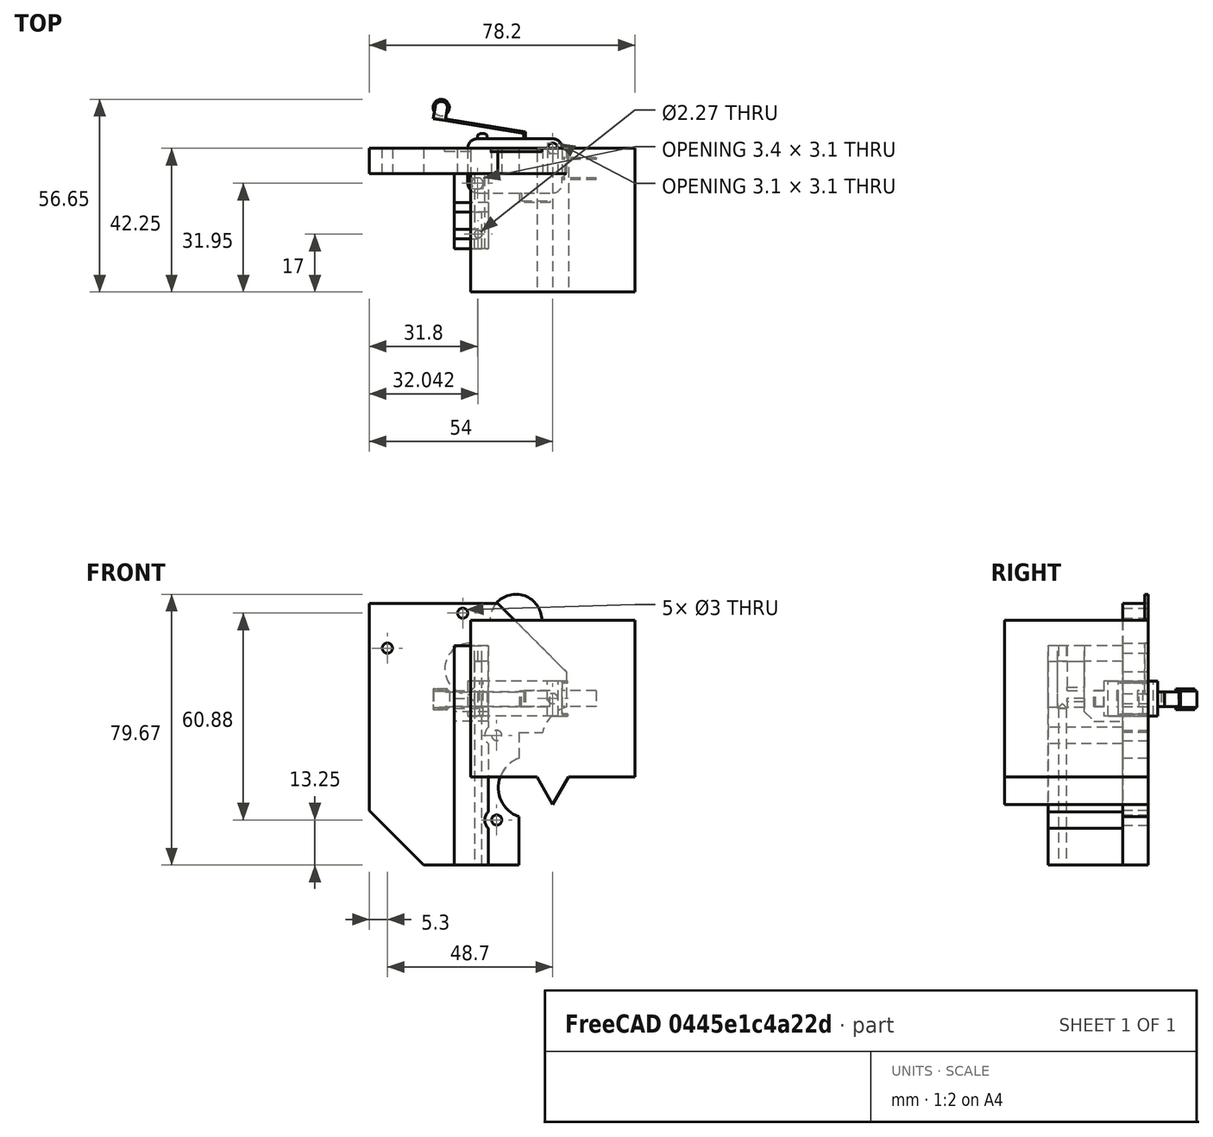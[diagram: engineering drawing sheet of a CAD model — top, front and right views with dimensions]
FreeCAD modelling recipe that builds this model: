
FCSTD DOCUMENT  (FreeCAD 0.19R22284 (Git))
Label: no_touchy
License: All rights reserved
LicenseURL: http://en.wikipedia.org/wiki/All_rights_reserved
objects: PartDesign::CoordinateSystem×15, Sketcher::SketchObject×14, PartDesign::Pad×6, PartDesign::Pocket×6, App::Part×6, App::Link×5, App::DocumentObjectGroup×2, Part::Feature×2, PartDesign::Body×2, PartDesign::Chamfer×2, App::FeaturePython×1, PartDesign::AdditivePipe×1, Spreadsheet::Sheet×1, Mesh::Feature×1
note: 63 computed .brp shape members not serialized (recipe doc carries the construction recipe); baked Part::Feature solids carry a one-line shape summary decoded from their .brp

FEATURE [PartDesign::CoordinateSystem] LCS_Origin
  AttacherType = Attacher::AttachEngine3D
  MapMode = 2
  Support = -> [X_Axis]
FEATURE [App::DocumentObjectGroup] Constraints
FEATURE [App::FeaturePython] Variables  # WARN: FeaturePython — macro-defined, semantics opaque (R4)
FEATURE [PartDesign::CoordinateSystem] LCS_0
  AttacherType = Attacher::AttachEngine3D
  MapMode = 2
  Support = -> [X_Axis001]
FEATURE [Sketcher::SketchObject] Sketch  label="hex"
  MapMode = 5
  Placement = pos=(0,0,0) rot=(0.57735,0.57735,0.57735;2.0944rad)
  expr: Constraints[19] = Spreadsheet.allen_key_hex
  sketch-geometry (7):
    g0: LineSegment StartX=0 StartY=0.733235 StartZ=0 EndX=-0.635 EndY=0.366617 EndZ=0
    g1: LineSegment StartX=-0.635 StartY=0.366617 StartZ=0 EndX=-0.635 EndY=-0.366617 EndZ=0
    g2: LineSegment StartX=-0.635 StartY=-0.366617 StartZ=0 EndX=0 EndY=-0.733235 EndZ=0
    g3: LineSegment StartX=0 StartY=-0.733235 StartZ=0 EndX=0.635 EndY=-0.366617 EndZ=0
    g4: LineSegment StartX=0.635 StartY=-0.366617 StartZ=0 EndX=0.635 EndY=0.366617 EndZ=0
    g5: LineSegment StartX=0.635 StartY=0.366617 StartZ=0 EndX=0 EndY=0.733235 EndZ=0
    g6: Circle [constr] CenterX=0 CenterY=0 CenterZ=0 NormalX=0 NormalY=0 NormalZ=1 AngleXU=0 Radius=0.733235
  constraints (16):
    c: Coincident(g0,g1)
    c: Coincident(g1,g2)
    c: Coincident(g2,g3)
    c: Coincident(g3,g4)
    c: Coincident(g4,g5)
    c: Coincident(g5,g0)
    c: Equal(g0, g1-g5) x5
    c: PointOnObject(g0,g6)
    c: PointOnObject(g1,g6)
    c: PointOnObject(g2,g6)
    c: PointOnObject(g3,g6)
    c: PointOnObject(g4,g6)
    c: PointOnObject(g5,g6)
    c: Coincident(g6,g-1)
    c: Vertical(g0,g-1)
    c: Distance(g3,g1) = 1.27
FEATURE [Sketcher::SketchObject] Sketch001  label="path"
  MapMode = 5
  expr: Constraints[5] = Spreadsheet.allen_key_long
  expr: Constraints[4] = Spreadsheet.allen_key_short
  sketch-geometry (3):
    g0: LineSegment StartX=0 StartY=-1.3e-15 StartZ=0 EndX=-12.3 EndY=-1.3e-15 EndZ=0
    g1: LineSegment StartX=-15.3 StartY=-3 StartZ=0 EndX=-15.3 EndY=-73.5 EndZ=0
    g2: ArcOfCircle CenterX=-12.3 CenterY=-3 CenterZ=0 NormalX=0 NormalY=0 NormalZ=1 AngleXU=0 Radius=3 StartAngle=1.5708 EndAngle=3.14159
  constraints (8):
    c: Coincident(g-1,g0)
    c: Vertical(g1)
    c: Tangent(g0,g2) = -1.5708
    c: Tangent(g1,g2) = -1.5708
    c: DistanceX(g1,g0) = 15.3
    c: DistanceY(g1,g0) = 73.5
    c: Horizontal(g0)
    c: Radius(g2) = 3
FEATURE [PartDesign::AdditivePipe] AdditivePipe
  AuxilleryCurvelinear = true
  AuxillerySpineTangent = false
  Binormal = (0,0,0)
  Mode = 0
  Placement = pos=(0,0,0) rot=(0.57735,0.57735,0.57735;2.0944rad)
  Profile = -> Sketch
  Spine = -> Sketch001
  SpineTangent = false
  Transformation = 0
  Transition = 0
FEATURE [Sketcher::SketchObject] Sketch002
  MapMode = 5
  Placement = pos=(0,0,0) rot=(1,0,0;1.5708rad)
  sketch-geometry (10):
    g0: LineSegment StartX=60 StartY=0 StartZ=0 EndX=0 EndY=0 EndZ=0
    g1: LineSegment StartX=0 StartY=0 StartZ=0 EndX=0 EndY=36.25 EndZ=0
    g2: LineSegment StartX=6.5 StartY=42.75 StartZ=0 EndX=11.5 EndY=42.75 EndZ=0
    g3: LineSegment StartX=18 StartY=49.25 StartZ=0 EndX=18 EndY=87.75 EndZ=0
    g4: LineSegment StartX=21 StartY=90.75 StartZ=0 EndX=57 EndY=90.75 EndZ=0
    g5: LineSegment StartX=60 StartY=87.75 StartZ=0 EndX=60 EndY=0 EndZ=0
    g6: ArcOfCircle CenterX=6.5 CenterY=36.25 CenterZ=0 NormalX=0 NormalY=0 NormalZ=1 AngleXU=0 Radius=6.5 StartAngle=1.5708 EndAngle=3.14159
    g7: ArcOfCircle CenterX=11.5 CenterY=49.25 CenterZ=0 NormalX=0 NormalY=0 NormalZ=1 AngleXU=0 Radius=6.5 StartAngle=4.71239 EndAngle=6.28319
    g8: ArcOfCircle CenterX=21 CenterY=87.75 CenterZ=0 NormalX=0 NormalY=0 NormalZ=1 AngleXU=0 Radius=3 StartAngle=1.5708 EndAngle=3.14159
    g9: ArcOfCircle CenterX=57 CenterY=87.75 CenterZ=0 NormalX=0 NormalY=0 NormalZ=1 AngleXU=0 Radius=3 StartAngle=1.2e-15 EndAngle=1.5708
  constraints (25):
    c: Horizontal(g0)
    c: Coincident(g0,g1)
    c: Vertical(g1)
    c: Horizontal(g2)
    c: Vertical(g3)
    c: Horizontal(g4)
    c: Coincident(g5,g0)
    c: Vertical(g5)
    c: Tangent(g2,g6) = 1.5708
    c: Tangent(g1,g6) = 1.5708
    c: Tangent(g2,g7) = -1.5708
    c: Tangent(g3,g7) = -1.5708
    c: DistanceY(g0,g2) = 42.75
    c: DistanceX(g1,g3) = 18
    c: DistanceX(g2,g2) = 5
    c: Equal(g6,g7)
    c: Coincident(g0,g-1)
    c: Tangent(g4,g8) = 1.5708
    c: Tangent(g3,g8) = 1.5708
    c: DistanceY(g2,g4) = 48
    c: Radius(g8) = 3
    c: Tangent(g4,g9) = 1.5708
    c: Tangent(g5,g9) = 1.5708
    c: Equal(g8,g9)
    c: DistanceX(g3,g5) = 42
FEATURE [PartDesign::Pad] Pad
  Length = 3.2
  Length2 = 100
  Placement = pos=(0,0,0) rot=(1,0,0;1.5708rad)
  Profile = -> Sketch002
  Type = 0
FEATURE [Sketcher::SketchObject] Sketch003
  ExternalGeometry = -> [Pad]
  MapMode = 5
  Placement = pos=(0,-3.2,1.1e-15) rot=(1,0,0;1.5708rad)
  Support = -> [Pad]
  sketch-geometry (8):
    g0: Circle CenterX=19.19 CenterY=39.94 CenterZ=0 NormalX=0 NormalY=0 NormalZ=1 AngleXU=0 Radius=1.19
    g1: Circle CenterX=2.69 CenterY=29.07 CenterZ=0 NormalX=0 NormalY=0 NormalZ=1 AngleXU=0 Radius=1.19
    g2: Circle CenterX=2.69 CenterY=4.19 CenterZ=0 NormalX=0 NormalY=0 NormalZ=1 AngleXU=0 Radius=1.19
    g3: LineSegment [constr] StartX=2.69 StartY=3 StartZ=0 EndX=2.69 EndY=0 EndZ=0
    g4: LineSegment [constr] StartX=2.69 StartY=27.88 StartZ=0 EndX=2.69 EndY=5.38 EndZ=0
    g5: LineSegment [constr] StartX=1.5 StartY=29.07 StartZ=0 EndX=0 EndY=29.07 EndZ=0
    g6: LineSegment [constr] StartX=18 StartY=39.94 StartZ=0 EndX=0 EndY=39.94 EndZ=0
    g7: LineSegment [constr] StartX=19.19 StartY=90.75 StartZ=0 EndX=19.19 EndY=38.75 EndZ=0
  constraints (29):
    c: Diameter(g0) = 2.38
    c: Equal(g0,g1)
    c: Equal(g1,g2)
    c: Vertical(g2,g1)
    c: Vertical(g3)
    c: Horizontal(g3,g-1)
    c: Vertical(g3,g2)
    c: PointOnObject(g3,g2)
    c: Distance(g3) = 3
    c: Vertical(g4)
    c: Distance(g4) = 22.5
    c: PointOnObject(g4,g2)
    c: Vertical(g4,g2)
    c: PointOnObject(g4,g1)
    c: Horizontal(g5)
    c: Horizontal(g5,g1)
    c: PointOnObject(g5,g1)
    c: Distance(g5) = 1.5
    c: PointOnObject(g5,g-3)
    c: Horizontal(g6)
    c: PointOnObject(g6,g0)
    c: Horizontal(g6,g0)
    c: Distance(g6) = 18
    c: Vertical(g6,g-3)
    c: Vertical(g7)
    c: Horizontal(g7,g-5)
    c: Distance(g7) = 52
    c: PointOnObject(g7,g0)
    c: Vertical(g0,g7)
FEATURE [PartDesign::Pocket] Pocket
  BaseFeature = -> Pad
  Length = 5
  Length2 = 100
  Placement = pos=(0,0,0) rot=(1,0,0;1.5708rad)
  Profile = -> Sketch003
  Type = 1
FEATURE [Part::Feature] Part__Feature001  label="V_166_1C25_ACTUATOR"
  Placement = pos=(-8.6,2.8,-0.2) rot=(0,0,1;0rad)
  shape: bbox 27.14 x 11.6 x 6 mm, 20 faces (baked)
FEATURE [Part::Feature] Part__Feature  label="V_166_1C25_BASE"
  shape: bbox 37.8 x 20.4 x 10.3 mm, 51 faces (baked)
FEATURE [Spreadsheet::Sheet] Spreadsheet
  cells = A1(limit_switch_mount_height)=5; A2(storage_ledge_height)=50; A3(probe_ledge_height)=25; A4(allen_key_long)=73.5; A5(allen_key_short)=15.3; A6(allen_key_hex)=1.27; A7(no_touchy_plate_mount_thickness)=7.5; A8(limit_switch_hole_offset_x)=-10; A9(limit_switch_hole_offset_y)=33; A10(no_touchy_allen_block_pad_height)=22; A11(no_touchy_allen_block_pad_length)=64.5; A12(no_touchy_allen_hole_length)=47.5; A13(no_touchy_allen_block_pad_width)=10; A14(no_touchy_allen_hole_diameter)==allen_key_hex + 1
FEATURE [PartDesign::CoordinateSystem] LCS_hole_1
  AttacherType = Attacher::AttachEngine3D
  AttachmentOffset = pos=(0,0,0) rot=(-0.57735,0.57735,-0.57735;2.0944rad)
  MapMode = 11
  Placement = pos=(0,0,-5.15) rot=(0,0.707107,-0.707107;3.14159rad)
  Support = -> [Part__Feature]
FEATURE [PartDesign::CoordinateSystem] LCS_hole_2
  AttacherType = Attacher::AttachEngine3D
  AttachmentOffset = pos=(0,0,0) rot=(0,-0.707107,0.707107;3.14159rad)
  MapMode = 45
  Placement = pos=(-22.2,-10.3,-5.15) rot=(0,-0.707107,0.707107;3.14159rad)
  Support = -> [Part__Feature]
FEATURE [PartDesign::CoordinateSystem] LCS_center
  AttacherType = Attacher::AttachEngine3D
  AttachmentOffset = pos=(0,0,0) rot=(0,0,1;3.14159rad)
  MapMode = 45
  Placement = pos=(-10.756,-5.10422,-5.15) rot=(0,0,1;4.67226rad)
  Support = -> [Part__Feature]
FEATURE [PartDesign::CoordinateSystem] LCS_allen_short_bottom_tip
  AttacherType = Attacher::AttachEngine3D
  MapMode = 45
  Placement = pos=(-1e-16,-0.635,-1e-16) rot=(0,0,1;0rad)
  Support = -> [AdditivePipe]
FEATURE [PartDesign::CoordinateSystem] LCS_allen_short_bottom_center
  AttacherType = Attacher::AttachEngine3D
  MapMode = 45
  Placement = pos=(-6.15,-0.635,-2e-16) rot=(0.57735,0.57735,0.57735;4.18879rad)
  Support = -> [AdditivePipe]
FEATURE [PartDesign::CoordinateSystem] LCS_allen_bottom_center
  AttacherType = Attacher::AttachEngine3D
  MapMode = 45
  Placement = pos=(-15.3,-73.5,-1.9e-15) rot=(0,0.707107,0.707107;3.14159rad)
  Support = -> [AdditivePipe]
FEATURE [Sketcher::SketchObject] Sketch004
  MapMode = 1
  Placement = pos=(0,0,0) rot=(1,0,0;1.5708rad)
  sketch-geometry (11):
    g0: LineSegment StartX=-24.2 StartY=23.075 StartZ=0 EndX=-18.45 EndY=23.075 EndZ=0
    g1: LineSegment StartX=24.2 StartY=23.075 StartZ=0 EndX=24.2 EndY=-23.075 EndZ=0
    g2: LineSegment StartX=24.2 StartY=-23.075 StartZ=0 EndX=4.67654 EndY=-23.075 EndZ=0
    g3: LineSegment StartX=-24.2 StartY=-23.075 StartZ=0 EndX=-24.2 EndY=1.125 EndZ=0
    g4: ArcOfCircle CenterX=-10.85 CenterY=23.075 CenterZ=0 NormalX=0 NormalY=0 NormalZ=1 AngleXU=0 Radius=7.6 StartAngle=0 EndAngle=3.14159
    g5: LineSegment StartX=-3.25 StartY=23.075 StartZ=0 EndX=24.2 EndY=23.075 EndZ=0
    g6: ArcOfCircle CenterX=-24.2 CenterY=8.725 CenterZ=0 NormalX=0 NormalY=0 NormalZ=1 AngleXU=0 Radius=7.6 StartAngle=1.5708 EndAngle=4.71239
    g7: LineSegment StartX=-24.2 StartY=16.325 StartZ=0 EndX=-24.2 EndY=23.075 EndZ=0
    g8: LineSegment StartX=-4.67654 StartY=-23.075 StartZ=0 EndX=5.338e-13 EndY=-31.175 EndZ=0
    g9: LineSegment StartX=4.67654 StartY=-23.075 StartZ=0 EndX=5.338e-13 EndY=-31.175 EndZ=0
    g10: LineSegment StartX=-4.67654 StartY=-23.075 StartZ=0 EndX=-24.2 EndY=-23.075 EndZ=0
  constraints (32):
    c: Coincident(g5,g1)
    c: Coincident(g1,g2)
    c: Coincident(g10,g3)
    c: Coincident(g7,g0)
    c: Horizontal(g0)
    c: Horizontal(g2)
    c: Vertical(g1)
    c: Vertical(g3)
    c: Tangent(g0,g5)
    c: Horizontal(g5,g4)
    c: Diameter(g4) = 15.2
    c: DistanceX(g0,g1) = 48.4
    c: Coincident(g4,g5)
    c: Coincident(g4,g0)
    c: PointOnObject(g6,g3)
    c: Coincident(g7,g6)
    c: Tangent(g3,g7)
    c: PointOnObject(g3,g6)
    c: Vertical(g6,g6)
    c: Diameter(g6) = 15.2
    c: DistanceY(g10,g0) = 46.15
    c: DistanceX(g0,g0) = 5.75
    c: DistanceY(g7,g7) = 6.75
    c: Coincident(g9,g8)
    c: Coincident(g2,g9)
    c: Coincident(g10,g8)
    c: Tangent(g2,g10)
    c: Angle(g9,g8) = 1.0472
    c: Equal(g9,g8)
    c: Distance(g8,g5) = 54.25
    c: Equal(g2,g10)
    c: Symmetric(g1,g3,g-1)
FEATURE [PartDesign::Pad] Pad001
  Length = 1
  Length2 = 100
  Placement = pos=(0,0,0) rot=(1,0,0;1.5708rad)
  Profile = -> Sketch004
  Type = 0
FEATURE [PartDesign::CoordinateSystem] LCS_hole_1001
  AttacherType = Attacher::AttachEngine3D
  AttachmentOffset = pos=(0,0,0) rot=(-0.57735,0.57735,-0.57735;2.0944rad)
  MapMode = 11
  Placement = pos=(19.19,-3.2,39.94) rot=(0,0,1;0rad)
  Support = -> [Pocket]
FEATURE [PartDesign::CoordinateSystem] LCS_hole_2001
  AttacherType = Attacher::AttachEngine3D
  AttachmentOffset = pos=(0,0,0) rot=(-0.57735,0.57735,-0.57735;2.0944rad)
  MapMode = 11
  Placement = pos=(2.69,-3.2,29.07) rot=(0,0,1;0rad)
  Support = -> [Pocket]
FEATURE [PartDesign::CoordinateSystem] LCS_hole_3
  AttacherType = Attacher::AttachEngine3D
  AttachmentOffset = pos=(0,0,0) rot=(-0.57735,0.57735,-0.57735;2.0944rad)
  MapMode = 11
  Placement = pos=(2.69,-3.2,4.19) rot=(0,0,1;0rad)
  Support = -> [Pocket]
FEATURE [PartDesign::CoordinateSystem] LCS_backplate_center
  AttacherType = Attacher::AttachEngine3D
  AttachmentOffset = pos=(0,0,0) rot=(1,0,0;1.5708rad)
  MapMode = 45
  Placement = pos=(41.2238,-3.2,43.8888) rot=(0,1,0;0.019094rad)
  Support = -> [Pocket]
FEATURE [App::Part] micro_swiss_direct_drive_backplate
  Group = -> [Sketch002,Pad,Sketch003,Pocket,LCS_backplate_center,LCS_hole_1001,LCS_hole_2001,LCS_hole_3]
  Origin = -> Origin002
FEATURE [App::Link] micro_swiss_direct_drive_backplate001
  AssemblyType = Asm4EE
  AttachedBy = #LCS_hole_1001
  AttachedTo = Parent Assembly#LCS_Origin
  LinkPlacement = pos=(-19.19,3.2,-39.94) rot=(0,0,1;0rad)
  LinkedObject = -> micro_swiss_direct_drive_backplate
  Placement = pos=(-19.19,3.2,-39.94) rot=(0,0,1;0rad)
  expr: Placement = LCS_Origin.Placement * AttachmentOffset * LCS_hole_1001.Placement ^ -1
FEATURE [App::Link] ender_3_fan_shroud001
  AssemblyType = Asm4EE
  AttachedBy = #LCS_0003
  AttachedTo = micro_swiss_direct_drive_backplate001#LCS_hole_2001
  AttachmentOffset = pos=(9.93,0,-1.18) rot=(0,0,1;0rad)
  LinkPlacement = pos=(17.63,-4.7e-15,-35.125) rot=(0,0,1;0rad)
  LinkedObject = -> ender_3_fan_shroud
  Placement = pos=(17.63,-4.7e-15,-35.125) rot=(0,0,1;0rad)
  expr: Placement = micro_swiss_direct_drive_backplate001.Placement * LCS_hole_2001.Placement * AttachmentOffset * LCS_0003.Placement ^ -1
FEATURE [PartDesign::CoordinateSystem] LCS_0004  label="LCS_no_touchy_hole_1"
  AttacherType = Attacher::AttachEngine3D
  MapMode = 2
  Support = -> [X_Axis007]
FEATURE [Sketcher::SketchObject] Sketch005
  MapMode = 5
  Placement = pos=(0,0,0) rot=(1,0,0;1.5708rad)
  Support = -> [XZ_Plane008]
  expr: Constraints[40] = -1 * Spreadsheet.limit_switch_hole_offset_x
  expr: Constraints[41] = -1 * Spreadsheet.limit_switch_hole_offset_y - 3
  sketch-geometry (16):
    g0: LineSegment StartX=-10 StartY=-9.95247 StartZ=0 EndX=-10 EndY=-17.609 EndZ=0
    g1: LineSegment StartX=-10 StartY=-49 StartZ=0 EndX=-38 EndY=-49 EndZ=0
    g2: LineSegment StartX=-54 StartY=-33 StartZ=0 EndX=-54 EndY=28 EndZ=0
    g3: LineSegment StartX=-54 StartY=28 StartZ=0 EndX=-16.1525 EndY=28 EndZ=0
    g4: LineSegment StartX=-10 StartY=-34.7961 StartZ=0 EndX=-10 EndY=-49 EndZ=0
    g5: LineSegment StartX=-10 StartY=-9.95247 StartZ=0 EndX=-2.95564 EndY=-9.95247 EndZ=0
    g6: LineSegment StartX=4 StartY=7.84746 StartZ=0 EndX=4 EndY=-2.5 EndZ=0
    g7: Circle CenterX=0 CenterY=0 CenterZ=0 NormalX=0 NormalY=0 NormalZ=1 AngleXU=0 Radius=2.25
    g8: Circle CenterX=-16.5 CenterY=-10.87 CenterZ=0 NormalX=0 NormalY=0 NormalZ=1 AngleXU=0 Radius=2.25
    g9: Circle CenterX=-16.5 CenterY=-35.75 CenterZ=0 NormalX=0 NormalY=0 NormalZ=1 AngleXU=0 Radius=2.25
    g10: ArcOfCircle CenterX=6.97621 CenterY=-12.25 CenterZ=0 NormalX=0 NormalY=0 NormalZ=1 AngleXU=0 Radius=10.1941 StartAngle=1.86706 EndAngle=2.91426
    g11: ArcOfCircle CenterX=-6.87222 CenterY=-26.2026 CenterZ=0 NormalX=0 NormalY=0 NormalZ=1 AngleXU=0 Radius=9.14502 StartAngle=1.91986 EndAngle=4.36332
    g12: LineSegment StartX=-54 StartY=-33 StartZ=0 EndX=-38 EndY=-49 EndZ=0
    g13: LineSegment StartX=-16.1525 StartY=28 StartZ=0 EndX=4 EndY=7.84746 EndZ=0
    g14: Circle CenterX=-26.5 CenterY=25.13 CenterZ=0 NormalX=0 NormalY=0 NormalZ=1 AngleXU=0 Radius=2.25
    g15: Circle CenterX=-48.7 CenterY=14.83 CenterZ=0 NormalX=0 NormalY=0 NormalZ=1 AngleXU=0 Radius=2.25
  constraints (50):
    c: Coincident(g4,g1)
    c: Horizontal(g1)
    c: Vertical(g0)
    c: Vertical(g2)
    c: Horizontal(g3)
    c: Coincident(g3,g2)
    c: Coincident(g5,g0)
    c: Coincident(g10,g6)
    c: Coincident(g10,g5)
    c: Angle(g10) = 1.0472
    c: Vertical(g6)
    c: Horizontal(g5)
    c: DistanceX(g8) = -16.5
    c: DistanceY(g8) = -10.87
    c: Radius(g7) = 2.25
    c: Equal(g8,g7)
    c: DistanceX(g9) = -16.5
    c: DistanceY(g9) = -35.75
    c: Equal(g9,g7)
    c: Coincident(g11,g0)
    c: Angle(g11) = 2.44346
    c: Vertical(g4)
    c: Coincident(g4,g11)
    c: Vertical(g4,g0)
    c: DistanceX(g7) = 0
    c: DistanceY(g7) = 0
    c: DistanceX(g4) = -10
    c: DistanceY(g4) = -34.7961
    c: DistanceX(g11) = -6.87222
    c: DistanceX(g10) = 6.97621
    c: DistanceY(g10) = -12.25
    c: DistanceX(g6) = 4
    c: DistanceY(g6) = -2.5
    c: Coincident(g12,g2)
    c: Coincident(g12,g1)
    c: Angle(g1,g12) = 2.35619
    c: Coincident(g13,g3)
    c: Coincident(g13,g6)
    c: Angle(g3,g13) = 2.35619
    c: Equal(g14,g7)
    c: DistanceX(g14,g8) = 10
    c: DistanceY(g14,g8) = -36
    c: Equal(g15,g7)
    c: DistanceX(g15,g14) = 22.2
    c: DistanceY(g15,g14) = 10.3
    c: DistanceX(g2) = -54
    c: DistanceY(g2) = 28
    c: DistanceX(g1) = -38
    c: DistanceY(g1) = -49
    c: Distance(g13) = 28.5
FEATURE [PartDesign::Pad] Pad002
  Length = 7.5
  Length2 = 100
  Placement = pos=(0,0,0) rot=(1,0,0;1.5708rad)
  Profile = -> Sketch005
  Type = 0
  expr: Length = Spreadsheet.no_touchy_plate_mount_thickness
FEATURE [App::Link] no_touchy001
  AssemblyType = Asm4EE
  AttachedBy = #LCS_0004
  AttachedTo = micro_swiss_direct_drive_backplate001#LCS_hole_1001
  LinkedObject = -> no_touchy
  expr: Placement = micro_swiss_direct_drive_backplate001.Placement * LCS_hole_1001.Placement * AttachmentOffset * LCS_0004.Placement ^ -1
FEATURE [Sketcher::SketchObject] Sketch006
  ExternalGeometry = -> [Pad001]
  MapMode = 5
  Placement = pos=(0,-1,3e-16) rot=(1,0,0;1.5708rad)
  Support = -> [Pad001]
  sketch-geometry (7):
    g0: LineSegment StartX=-24.2 StartY=23.075 StartZ=0 EndX=24.2 EndY=23.075 EndZ=0
    g1: LineSegment StartX=24.2 StartY=23.075 StartZ=0 EndX=24.2 EndY=-23.075 EndZ=0
    g2: LineSegment StartX=-24.2 StartY=-23.075 StartZ=0 EndX=-24.2 EndY=23.075 EndZ=0
    g3: LineSegment StartX=-24.2 StartY=-23.075 StartZ=0 EndX=-4.67654 EndY=-23.075 EndZ=0
    g4: LineSegment StartX=-4.67654 StartY=-23.075 StartZ=0 EndX=5.338e-13 EndY=-31.175 EndZ=0
    g5: LineSegment StartX=5.338e-13 StartY=-31.175 StartZ=0 EndX=4.67654 EndY=-23.075 EndZ=0
    g6: LineSegment StartX=4.67654 StartY=-23.075 StartZ=0 EndX=24.2 EndY=-23.075 EndZ=0
  constraints (15):
    c: Coincident(g0,g1)
    c: Coincident(g2,g0)
    c: Horizontal(g0)
    c: Vertical(g1)
    c: Coincident(g2,g3)
    c: Coincident(g3,g4)
    c: Coincident(g4,g5)
    c: Coincident(g5,g6)
    c: Coincident(g6,g1)
    c: Coincident(g1,g-4)
    c: Coincident(g5,g-5)
    c: Coincident(g4,g-6)
    c: Coincident(g3,g-7)
    c: Coincident(g2,g-8)
    c: Coincident(g0,g-3)
FEATURE [PartDesign::Pad] Pad003
  BaseFeature = -> Pad001
  Length = 41.25
  Length2 = 100
  Placement = pos=(0,0,0) rot=(1,0,0;1.5708rad)
  Profile = -> Sketch006
  Type = 0
FEATURE [PartDesign::Body] Body001
  Group = -> [Pad001,Sketch004,Sketch006,Pad003]
  Origin = -> Origin009
  Tip = -> Pad003
FEATURE [App::Part] ender_3_fan_shroud
  Group = -> [Body001]
  Origin = -> Origin006
FEATURE [App::Link] limit_switch001
  AssemblyType = Asm4EE
  AttachedBy = #LCS_hole_2
  AttachedTo = micro_swiss_direct_drive_backplate001#LCS_hole_2001
  AttachmentOffset = pos=(-10,-7.5,33) rot=(0,0,1;0rad)
  LinkPlacement = pos=(-48.7,-12.65,11.83) rot=(0,0.707107,-0.707107;3.14159rad)
  LinkedObject = -> limit_switch
  Placement = pos=(-48.7,-12.65,11.83) rot=(0,0.707107,-0.707107;3.14159rad)
  expr: .AttachmentOffset.Base.z = Spreadsheet.limit_switch_hole_offset_y
  expr: .AttachmentOffset.Base.x = Spreadsheet.limit_switch_hole_offset_x
  expr: .AttachmentOffset.Base.y = -1 * Spreadsheet.no_touchy_plate_mount_thickness
  expr: Placement = micro_swiss_direct_drive_backplate001.Placement * LCS_hole_2001.Placement * AttachmentOffset * LCS_hole_2.Placement ^ -1
FEATURE [PartDesign::CoordinateSystem] LCS_allen_touch
  AttacherType = Attacher::AttachEngine3D
  AttachmentOffset = pos=(19,0,0) rot=(0,1,0;0.15708rad)
  MapMode = 5
  Placement = pos=(-27.0186,7.91522,-0.2) rot=(0.00132,0.707106,0.707106;3.13895rad)
  Support = -> [Part__Feature001]
FEATURE [App::Part] limit_switch
  Group = -> [Part__Feature001,Part__Feature,LCS_hole_1,LCS_hole_2,LCS_center,LCS_allen_touch]
  Origin = -> Origin003
  Placement = pos=(-53,-13,2.9e-15) rot=(0,-0.707107,0.707107;3.14159rad)
FEATURE [PartDesign::CoordinateSystem] LCS_allen_short_top_tip
  AttacherType = Attacher::AttachEngine3D
  MapMode = 45
  Placement = pos=(1e-16,0.635,1e-16) rot=(0,0,1;0rad)
  Support = -> [AdditivePipe]
FEATURE [App::Part] Allen  label="allen"
  Group = -> [LCS_0,Sketch,Sketch001,AdditivePipe,LCS_allen_short_bottom_tip,LCS_allen_short_bottom_center,LCS_allen_bottom_center,LCS_allen_short_top_tip]
  Origin = -> Origin001
FEATURE [App::Link] allen  label="allen001"
  AssemblyType = Asm4EE
  AttachedBy = #LCS_allen_short_top_tip
  AttachedTo = limit_switch001#LCS_allen_touch
  AttachmentOffset = pos=(0,-2.5,0) rot=(-0.57735,0.57735,-0.57735;2.0944rad)
  LinkPlacement = pos=(-21.6838,-9.95,3.27979) rot=(0.578068,0.578068,0.575913;2.09655rad)
  LinkedObject = -> Allen
  Placement = pos=(-21.6838,-9.95,3.27979) rot=(0.578068,0.578068,0.575913;2.09655rad)
  expr: Placement = limit_switch001.Placement * LCS_allen_touch.Placement * AttachmentOffset * LCS_allen_short_top_tip.Placement ^ -1
FEATURE [App::Part] Model
  Configuration = 0
  Group = -> [LCS_Origin,Constraints,Variables,micro_swiss_direct_drive_backplate001,ender_3_fan_shroud001,no_touchy001,limit_switch001,allen]
  Origin = -> Origin
  Type = Assembly4 Model
FEATURE [Sketcher::SketchObject] Sketch007
  ExternalGeometry = -> [Pad002]
  MapMode = 5
  Placement = pos=(0,-7.5,-1.7e-15) rot=(1,0,0;1.5708rad)
  Support = -> [Pad002]
  expr: Constraints[21] = Spreadsheet.no_touchy_allen_block_pad_width
  expr: Constraints[19] = Spreadsheet.no_touchy_allen_block_pad_length
  sketch-geometry (8):
    g0: LineSegment StartX=-29 StartY=15.5 StartZ=0 EndX=-19 EndY=15.5 EndZ=0
    g1: LineSegment StartX=-19 StartY=15.5 StartZ=0 EndX=-19 EndY=-8.42046 EndZ=0
    g2: LineSegment StartX=-19 StartY=-49 StartZ=0 EndX=-29 EndY=-49 EndZ=0
    g3: LineSegment StartX=-29 StartY=-49 StartZ=0 EndX=-29 EndY=15.5 EndZ=0
    g4: ArcOfCircle CenterX=-16.5 CenterY=-10.87 CenterZ=0 NormalX=0 NormalY=0 NormalZ=1 AngleXU=0 Radius=3.5 StartAngle=2.3664 EndAngle=3.91679
    g5: LineSegment StartX=-19 StartY=-13.3194 StartZ=0 EndX=-19 EndY=-33.3005 EndZ=0
    g6: ArcOfCircle CenterX=-16.5 CenterY=-35.75 CenterZ=0 NormalX=0 NormalY=0 NormalZ=1 AngleXU=0 Radius=3.5 StartAngle=2.3664 EndAngle=3.91679
    g7: LineSegment StartX=-19 StartY=-38.1995 StartZ=0 EndX=-19 EndY=-49 EndZ=0
  constraints (22):
    c: Coincident(g0,g1)
    c: Coincident(g7,g2)
    c: Coincident(g2,g3)
    c: Coincident(g3,g0)
    c: Horizontal(g0)
    c: Horizontal(g2)
    c: Vertical(g1)
    c: Vertical(g3)
    c: Horizontal(g2,g-3)
    c: Coincident(g4,g-5)
    c: Coincident(g1,g4)
    c: Coincident(g5,g4)
    c: Tangent(g1,g5)
    c: Coincident(g6,g-4)
    c: Coincident(g5,g6)
    c: Coincident(g7,g6)
    c: Tangent(g5,g7)
    c: Equal(g6,g4)
    c: Radius(g4) = 3.5
    c: DistanceY(g3,g3) = 64.5
    c: DistanceX(g0,g4) = 2.5
    c: DistanceX(g2,g2) = 10
FEATURE [PartDesign::Pad] Pad004
  BaseFeature = -> Pad002
  Length = 22
  Length2 = 100
  Placement = pos=(0,0,0) rot=(1,0,0;1.5708rad)
  Profile = -> Sketch007
  Type = 0
  expr: Length = Spreadsheet.no_touchy_allen_block_pad_height
FEATURE [Sketcher::SketchObject] Sketch008
  ExternalGeometry = -> [Pad004]
  MapMode = 5
  Placement = pos=(0,-1.09e-14,-49) rot=(1,0,0;3.14159rad)
  Support = -> [Pad004]
  expr: Constraints[0] = Spreadsheet.no_touchy_allen_hole_diameter
  sketch-geometry (1):
    g0: Circle CenterX=-21.958 CenterY=25.2495 CenterZ=0 NormalX=0 NormalY=0 NormalZ=1 AngleXU=0 Radius=1.135
  constraints (3):
    c: Diameter(g0) = 2.27
    c: DistanceX(g0,g-3) = 3.95804
    c: DistanceY(g0,g-3) = -25.2495
FEATURE [PartDesign::Pocket] Pocket001  label="Pocket_allen_hole"
  BaseFeature = -> Pad004
  Length = 1
  Length2 = 100
  Placement = pos=(0,0,0) rot=(1,0,0;1.5708rad)
  Profile = -> Sketch008
  Type = 1
FEATURE [Sketcher::SketchObject] Sketch009
  ExternalGeometry = -> [Pocket001]
  MapMode = 5
  Placement = pos=(0,-29.5,1e-16) rot=(1,0,0;1.5708rad)
  Support = -> [Pocket001]
  sketch-geometry (4):
    g0: LineSegment StartX=-20.823 StartY=11 StartZ=0 EndX=-23.093 EndY=11 EndZ=0
    g1: LineSegment StartX=-23.093 StartY=11 StartZ=0 EndX=-23.093 EndY=-1.5 EndZ=0
    g2: LineSegment StartX=-20.823 StartY=-1.5 StartZ=0 EndX=-20.823 EndY=11 EndZ=0
    g3: ArcOfCircle CenterX=-21.958 CenterY=-1.5 CenterZ=0 NormalX=0 NormalY=0 NormalZ=1 AngleXU=0 Radius=1.135 StartAngle=3.14159 EndAngle=6.28319
  constraints (13):
    c: Coincident(g0,g1)
    c: Coincident(g2,g0)
    c: Horizontal(g0)
    c: Vertical(g1)
    c: Vertical(g2)
    c: Vertical(g2,g-3)
    c: Vertical(g1,g-3)
    c: Coincident(g3,g2)
    c: Coincident(g3,g1)
    c: Horizontal(g2,g1)
    c: Horizontal(g1,g3)
    c: DistanceY(g-3,g1) = 47.5
    c: DistanceY(g-3,g0) = 60
FEATURE [PartDesign::Pocket] Pocket002  label="Pocket_allen_short_slot"
  BaseFeature = -> Pocket001
  Length = 22
  Length2 = 100
  Placement = pos=(0,0,0) rot=(1,0,0;1.5708rad)
  Profile = -> Sketch009
  Type = 0
  expr: Length = Spreadsheet.no_touchy_allen_block_pad_height
FEATURE [Sketcher::SketchObject] Sketch010
  ExternalGeometry = -> [Pocket002]
  MapMode = 5
  Placement = pos=(-19,0,0) rot=(0.707107,0,0.707107;3.14159rad)
  Support = -> [Pocket002]
  sketch-geometry (5):
    g0: LineSegment StartX=-3.85471 StartY=18.7661 StartZ=0 EndX=15.5 EndY=18.7661 EndZ=0
    g1: LineSegment StartX=15.5 StartY=18.7661 StartZ=0 EndX=15.5 EndY=7.5 EndZ=0
    g2: LineSegment StartX=15.5 StartY=7.5 StartZ=0 EndX=-6.68553 EndY=7.5 EndZ=0
    g3: LineSegment StartX=-6.68553 StartY=7.5 StartZ=0 EndX=-6.68553 EndY=15.9352 EndZ=0
    g4: LineSegment StartX=-6.68553 StartY=15.9352 StartZ=0 EndX=-3.85471 EndY=18.7661 EndZ=0
  constraints (12):
    c: Coincident(g1,g2)
    c: Horizontal(g0)
    c: Horizontal(g2)
    c: Vertical(g1)
    c: Vertical(g3)
    c: Coincident(g3,g2)
    c: Horizontal(g1,g-4)
    c: Coincident(g1,g0)
    c: Vertical(g1,g-4)
    c: Coincident(g3,g4)
    c: Coincident(g0,g4)
    c: Angle(g3,g4) = 2.35619
FEATURE [PartDesign::Pocket] Pocket003  label="Pocket_limit_switch_actuator"
  BaseFeature = -> Pocket002
  Length = 5
  Length2 = 100
  Placement = pos=(0,0,0) rot=(1,0,0;1.5708rad)
  Profile = -> Sketch010
  Type = 1
FEATURE [Sketcher::SketchObject] Sketch011
  ExternalGeometry = -> [Pocket003]
  MapMode = 5
  Placement = pos=(-29,0,0) rot=(0.707107,0,-0.707107;3.14159rad)
  Support = -> [Pocket003]
  sketch-geometry (4):
    g0: LineSegment StartX=-15.5 StartY=23.8145 StartZ=0 EndX=2.935 EndY=23.8145 EndZ=0
    g1: LineSegment StartX=2.935 StartY=23.8145 StartZ=0 EndX=2.935 EndY=26.6845 EndZ=0
    g2: LineSegment StartX=2.935 StartY=26.6845 StartZ=0 EndX=-15.5 EndY=26.6845 EndZ=0
    g3: LineSegment StartX=-15.5 StartY=26.6845 StartZ=0 EndX=-15.5 EndY=23.8145 EndZ=0
  constraints (7):
    c: Coincident(g0,g1)
    c: Coincident(g1,g2)
    c: Coincident(g2,g3)
    c: Coincident(g3,g0)
    c: Horizontal(g0)
    c: Vertical(g1)
    c: Vertical(g3)
FEATURE [PartDesign::Pocket] Pocket004  label="Pocket_allen_insert_1"
  BaseFeature = -> Pocket003
  Length = 7
  Length2 = 100
  Placement = pos=(0,0,0) rot=(1,0,0;1.5708rad)
  Profile = -> Sketch011
  Type = 0
FEATURE [Sketcher::SketchObject] Sketch012
  ExternalGeometry = -> [Pocket004]
  MapMode = 5
  Placement = pos=(-29,0,0) rot=(0.707107,0,-0.707107;3.14159rad)
  Support = -> [Pocket004]
  expr: Constraints[10] = Spreadsheet.no_touchy_allen_hole_diameter
  sketch-geometry (4):
    g0: LineSegment StartX=-2.335 StartY=18.7661 StartZ=0 EndX=-0.065 EndY=18.7661 EndZ=0
    g1: LineSegment StartX=-0.065 StartY=18.7661 StartZ=0 EndX=-0.065 EndY=23.8145 EndZ=0
    g2: LineSegment StartX=-0.065 StartY=23.8145 StartZ=0 EndX=-2.335 EndY=23.8145 EndZ=0
    g3: LineSegment StartX=-2.335 StartY=23.8145 StartZ=0 EndX=-2.335 EndY=18.7661 EndZ=0
  constraints (12):
    c: Coincident(g0,g1)
    c: Coincident(g1,g2)
    c: Coincident(g2,g3)
    c: Coincident(g3,g0)
    c: Horizontal(g0)
    c: Horizontal(g2)
    c: Vertical(g1)
    c: Vertical(g3)
    c: Horizontal(g1,g-3)
    c: Horizontal(g0,g-4)
    c: DistanceX(g2,g2) = 2.27
    c: DistanceX(g1,g-3) = 3
FEATURE [PartDesign::Pocket] Pocket005  label="Pocket_allen_insert_2"
  BaseFeature = -> Pocket004
  Length = 5
  Length2 = 100
  Placement = pos=(0,0,0) rot=(1,0,0;1.5708rad)
  Profile = -> Sketch012
  Type = 2
FEATURE [PartDesign::Chamfer] Chamfer
  Angle = 45
  Base = -> Pocket005 [Edge145]
  BaseFeature = -> Pocket005
  ChamferType = 0
  FlipDirection = false
  Placement = pos=(0,0,0) rot=(1,0,0;1.5708rad)
  Size = 1
  Size2 = 1
  SupportTransform = false
FEATURE [PartDesign::Chamfer] Chamfer001
  Angle = 45
  Base = -> Chamfer [Edge59]
  BaseFeature = -> Chamfer
  ChamferType = 0
  FlipDirection = false
  Placement = pos=(0,0,0) rot=(1,0,0;1.5708rad)
  Size = 1
  Size2 = 1
  SupportTransform = false
FEATURE [Sketcher::SketchObject] Sketch013
  ExternalGeometry = -> [Chamfer001]
  MapMode = 5
  Placement = pos=(0,-7.5,1.7e-15) rot=(1,0,0;1.5708rad)
  Support = -> [Chamfer001]
  sketch-geometry (4):
    g0: LineSegment StartX=-23.093 StartY=15.5 StartZ=0 EndX=-19 EndY=15.5 EndZ=0
    g1: LineSegment StartX=-19 StartY=15.5 StartZ=0 EndX=-19 EndY=11 EndZ=0
    g2: LineSegment StartX=-19 StartY=11 StartZ=0 EndX=-23.093 EndY=11 EndZ=0
    g3: LineSegment StartX=-23.093 StartY=11 StartZ=0 EndX=-23.093 EndY=15.5 EndZ=0
  constraints (10):
    c: Coincident(g0,g1)
    c: Coincident(g1,g2)
    c: Coincident(g2,g3)
    c: Coincident(g3,g0)
    c: Horizontal(g0)
    c: Horizontal(g2)
    c: Vertical(g1)
    c: Vertical(g3)
    c: Coincident(g0,g-3)
    c: Coincident(g2,g-4)
FEATURE [PartDesign::Pad] Pad005  label="Pad_support_allen_block"
  BaseFeature = -> Chamfer001
  Length = 10
  Length2 = 100
  Placement = pos=(0,0,0) rot=(1,0,0;1.5708rad)
  Profile = -> Sketch013
  Type = 2
FEATURE [PartDesign::Body] Body
  Group = -> [Sketch005,Pad002,Sketch007,Pad004,Sketch008,Pocket001,Sketch009,Pocket002,Sketch010,Pocket003,Sketch011,Pocket004,Sketch012,Pocket005,Chamfer,Chamfer001,Sketch013,Pad005]
  Origin = -> Origin008
  Tip = -> Pad005
FEATURE [App::Part] no_touchy
  Group = -> [LCS_0004,Body]
  Origin = -> Origin007
FEATURE [App::DocumentObjectGroup] Parts
  Group = -> [Allen,micro_swiss_direct_drive_backplate,limit_switch,ender_3_fan_shroud,no_touchy]
FEATURE [Mesh::Feature] Mesh  label="no_touchy (Meshed)"
  Placement = pos=(0,0,113) rot=(0,0,1;0rad)
